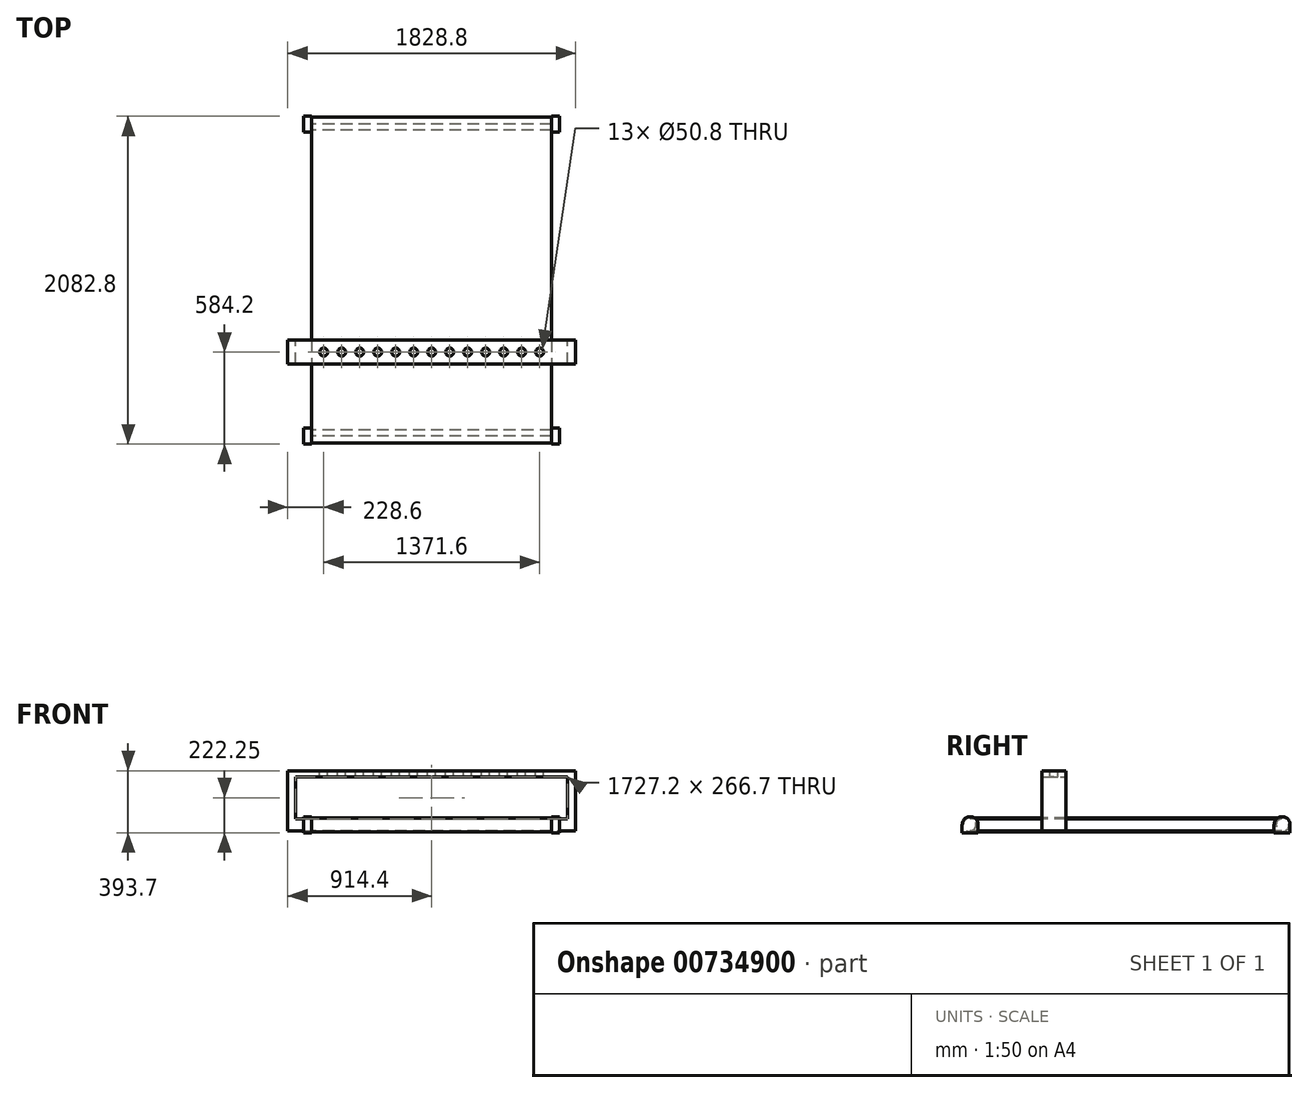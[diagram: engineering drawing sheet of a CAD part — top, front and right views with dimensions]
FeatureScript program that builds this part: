
annotation { "Feature Type Name" : "Feature", "Feature Type Description" : "" }
export const myFeature = defineFeature(function(context is Context, id is Id, definition is map)
    precondition{}
    {
        {
            var Q0;
            Q0=qCreatedBy(makeId("Right.planeOp"),FACE);
            var sketch = newSketch(context, id + "F0", { "sketchPlane" : qUnion([Q0])});
            skLineSegment(sketch, "E0.bottom", {"start": v(990.6, 38.1) * mm, "end": v(-990.6, 38.1) * mm});
            skLineSegment(sketch, "E0.top", {"start": v(990.6, -38.1) * mm, "end": v(-990.6, -38.1) * mm});
            skPoint(sketch, "E0.middle", {"position": v(0, 0) * mm});
            skArc(sketch, "E1", {"start": v(990.6, 38.1) * mm, "mid": v(1028.7, 0) * mm, "end": v(990.6, -38.1) * mm});
            skArc(sketch, "E2", {"start": v(-990.6, -38.1) * mm, "mid": v(-1028.7, 0) * mm, "end": v(-990.6, 38.1) * mm});
            skLineSegment(sketch, "E3.0", {"start": v(990.6, 44.45) * mm, "end": v(-990.6, 44.45) * mm});
            skArc(sketch, "E3.1", {"start": v(990.6, 44.45) * mm, "mid": v(1035.05, 0) * mm, "end": v(990.6, -44.45) * mm});
            skLineSegment(sketch, "E3.2", {"start": v(990.6, -44.45) * mm, "end": v(-990.6, -44.45) * mm});
            skArc(sketch, "E3.3", {"start": v(-990.6, -44.45) * mm, "mid": v(-1035.05, 0) * mm, "end": v(-990.6, 44.45) * mm});
            skSolve(sketch);
        }
        {
            var Q0;
            Q0 = qSketchRegion(id + "F0", true);
            extrude(context, id + "F1", {"entities" : qUnion([Q0]), "endBound" : BoundingType.SYMMETRIC, "depth" : 1524 * mm, "offsetDistance" : 25.4 * mm});
        }
        {
            var Q0;
            Q0=qCreatedBy(makeId("Right.planeOp"),FACE);
            var sketch = newSketch(context, id + "F2", { "sketchPlane" : qUnion([Q0])});
            skCircle(sketch, "E4", {"center": v(-990.6, 0) * mm, "radius": 38.1 * mm});
            skCircle(sketch, "E5", {"center": v(990.6, 0) * mm, "radius": 38.1 * mm});
            skSolve(sketch);
        }
        {
            var Q0;
            Q0 = qSketchRegion(id + "F2", true);
            extrude(context, id + "F3", {"entities" : qUnion([Q0]), "operationType" : NewBodyOperationType.ADD, "endBound" : BoundingType.SYMMETRIC, "depth" : 1625.6 * mm, "offsetDistance" : 25.4 * mm});
        }
        {
            var Q0;
            Q0=makeQuery(id+"F1.opExtrude","CAP_FACE",FACE,{"disambiguationData":[OSD([sQuery(id+"F0.wireOp",EDGE,"E0.bottom"),sQuery(id+"F0.wireOp",EDGE,"E0.top"),sQuery(id+"F0.wireOp",EDGE,"E1"),sQuery(id+"F0.wireOp",EDGE,"E2"),sQuery(id+"F0.wireOp",EDGE,"E3.0"),sQuery(id+"F0.wireOp",EDGE,"E3.1"),sQuery(id+"F0.wireOp",EDGE,"E3.2"),sQuery(id+"F0.wireOp",EDGE,"E3.3")])],"isStart":false});
            var sketch = newSketch(context, id + "F4", { "sketchPlane" : qUnion([Q0])});
            skArc(sketch, "E6", {"start": v(-939.8, 0) * mm, "mid": v(-990.6, 50.8) * mm, "end": v(-1041.4, 0) * mm});
            skCircle(sketch, "E7", {"center": v(-990.6, 0) * mm, "radius": 38.1 * mm});
            skLineSegment(sketch, "E8.top", {"start": v(-1041.4, -50.8) * mm, "end": v(-939.8, -50.8) * mm});
            skLineSegment(sketch, "E8.left", {"start": v(-1041.4, 0) * mm, "end": v(-1041.4, -50.8) * mm});
            skLineSegment(sketch, "E8.right", {"start": v(-939.8, 0) * mm, "end": v(-939.8, -50.8) * mm});
            skSolve(sketch);
        }
        {
            var Q0;
            Q0 = qSketchRegion(id + "F4", true);
            var Q1;
            Q1=makeQuery(id+"F3.opExtrude","CAP_FACE",FACE,{"disambiguationData":[OSD([sQuery(id+"F2.wireOp",EDGE,"E4")])],"isStart":false});
            extrude(context, id + "F5", {"entities" : qUnion([Q0]), "operationType" : NewBodyOperationType.ADD, "endBound" : BoundingType.UP_TO_SURFACE, "depth" : 25.4 * mm, "endBoundEntityFace" : qUnion([Q1]), "offsetDistance" : 25.4 * mm});
        }
        {
            var Q0;
            Q0=makeQuery(id+"F1.opExtrude","SWEPT_BODY",BODY,{"disambiguationData":[OSD([sQuery(id+"F0.wireOp",EDGE,"E0.bottom"),sQuery(id+"F0.wireOp",EDGE,"E0.top"),sQuery(id+"F0.wireOp",EDGE,"E1"),sQuery(id+"F0.wireOp",EDGE,"E2"),sQuery(id+"F0.wireOp",EDGE,"E3.0"),sQuery(id+"F0.wireOp",EDGE,"E3.1"),sQuery(id+"F0.wireOp",EDGE,"E3.2"),sQuery(id+"F0.wireOp",EDGE,"E3.3")])]});
            var Q1;
            Q1=qCreatedBy(makeId("Right.planeOp"),FACE);
            mirror(context, id + "F6", {"operationType" : NewBodyOperationType.ADD, "entities" : qUnion([Q0]), "mirrorPlane" : qUnion([Q1])});
        }
        {
            var Q0;
            Q0=makeQuery(id+"F1.opExtrude","SWEPT_BODY",BODY,{"disambiguationData":[OSD([sQuery(id+"F0.wireOp",EDGE,"E0.bottom"),sQuery(id+"F0.wireOp",EDGE,"E0.top"),sQuery(id+"F0.wireOp",EDGE,"E1"),sQuery(id+"F0.wireOp",EDGE,"E2"),sQuery(id+"F0.wireOp",EDGE,"E3.0"),sQuery(id+"F0.wireOp",EDGE,"E3.1"),sQuery(id+"F0.wireOp",EDGE,"E3.2"),sQuery(id+"F0.wireOp",EDGE,"E3.3")])]});
            var Q1;
            Q1=qCreatedBy(makeId("Front.planeOp"),FACE);
            mirror(context, id + "F7", {"operationType" : NewBodyOperationType.ADD, "entities" : qUnion([Q0]), "mirrorPlane" : qUnion([Q1])});
        }
        {
            var Q0;
            Q0=qCreatedBy(makeId("Front.planeOp"),FACE);
            cPlane(context, id + "F8", {"entities" : qUnion([Q0]), "cplaneType" : CPlaneType.OFFSET, "offset" : 457.2 * mm, "width" : 152.4 * mm, "height" : 152.4 * mm});
        }
        {
            var Q0;
            Q0=qCreatedBy(id+"F8.planeOp",FACE);
            var sketch = newSketch(context, id + "F9", { "sketchPlane" : qUnion([Q0])});
            skLineSegment(sketch, "E9.bottom", {"start": v(-863.6, 38.1) * mm, "end": v(863.6, 38.1) * mm});
            skLineSegment(sketch, "E9.top", {"start": v(-914.4, -38.1) * mm, "end": v(914.4, -38.1) * mm});
            skLineSegment(sketch, "E10.right", {"start": v(-863.6, 38.1) * mm, "end": v(-863.6, 304.8) * mm});
            skLineSegment(sketch, "E11.right", {"start": v(863.6, 38.1) * mm, "end": v(863.6, 304.8) * mm});
            skLineSegment(sketch, "E12.bottom", {"start": v(863.6, 304.8) * mm, "end": v(-863.6, 304.8) * mm});
            skLineSegment(sketch, "E12.top", {"start": v(914.4, 342.9) * mm, "end": v(-914.4, 342.9) * mm});
            skLineSegment(sketch, "E13", {"start": v(914.4, 342.9) * mm, "end": v(914.4, -38.1) * mm});
            skLineSegment(sketch, "E14", {"start": v(-914.4, 342.9) * mm, "end": v(-914.4, -38.1) * mm});
            skSolve(sketch);
        }
        {
            var Q0;
            Q0 = qSketchRegion(id + "F9", true);
            extrude(context, id + "F10", {"entities" : qUnion([Q0]), "endBound" : BoundingType.SYMMETRIC, "depth" : 152.4 * mm, "offsetDistance" : 25.4 * mm});
        }
        {
            var Q0;
            Q0=makeQuery(id+"F10.opExtrude","SWEPT_FACE",FACE,{"disambiguationData":[OSD([sQuery(id+"F9.wireOp",EDGE,"E12.top")])]});
            var sketch = newSketch(context, id + "F11", { "sketchPlane" : qUnion([Q0])});
            skCircle(sketch, "E15", {"center": v(-457.2, -457.2) * mm, "radius": 25.4 * mm});
            skPoint(sketch, "E16.middle", {"position": v(0, -457.2) * mm});
            skCircle(sketch, "E17", {"center": v(0, -457.2) * mm, "radius": 25.4 * mm});
            skCircle(sketch, "E18", {"center": v(-342.9, -457.2) * mm, "radius": 25.4 * mm});
            skCircle(sketch, "E19", {"center": v(-114.3, -457.2) * mm, "radius": 25.4 * mm});
            skCircle(sketch, "E20", {"center": v(-228.6, -457.2) * mm, "radius": 25.4 * mm});
            skCircle(sketch, "E21", {"center": v(-571.5, -457.2) * mm, "radius": 25.4 * mm});
            skCircle(sketch, "E22", {"center": v(-685.8, -457.2) * mm, "radius": 25.4 * mm});
            skCircle(sketch, "E23.MirrorC", {"center": v(114.3, -457.2) * mm, "radius": 25.4 * mm});
            skCircle(sketch, "E24.MirrorC", {"center": v(228.6, -457.2) * mm, "radius": 25.4 * mm});
            skCircle(sketch, "E25.MirrorC", {"center": v(342.9, -457.2) * mm, "radius": 25.4 * mm});
            skCircle(sketch, "E26.MirrorC", {"center": v(457.2, -457.2) * mm, "radius": 25.4 * mm});
            skCircle(sketch, "E27.MirrorC", {"center": v(571.5, -457.2) * mm, "radius": 25.4 * mm});
            skCircle(sketch, "E28.MirrorC", {"center": v(685.8, -457.2) * mm, "radius": 25.4 * mm});
            skSolve(sketch);
        }
        {
            var Q0;
            Q0 = qSketchRegion(id + "F11", true);
            extrude(context, id + "F12", {"entities" : qUnion([Q0]), "operationType" : NewBodyOperationType.REMOVE, "endBound" : BoundingType.UP_TO_NEXT, "oppositeDirection" : true, "depth" : 25.4 * mm, "offsetDistance" : 25.4 * mm});
        }
    });
